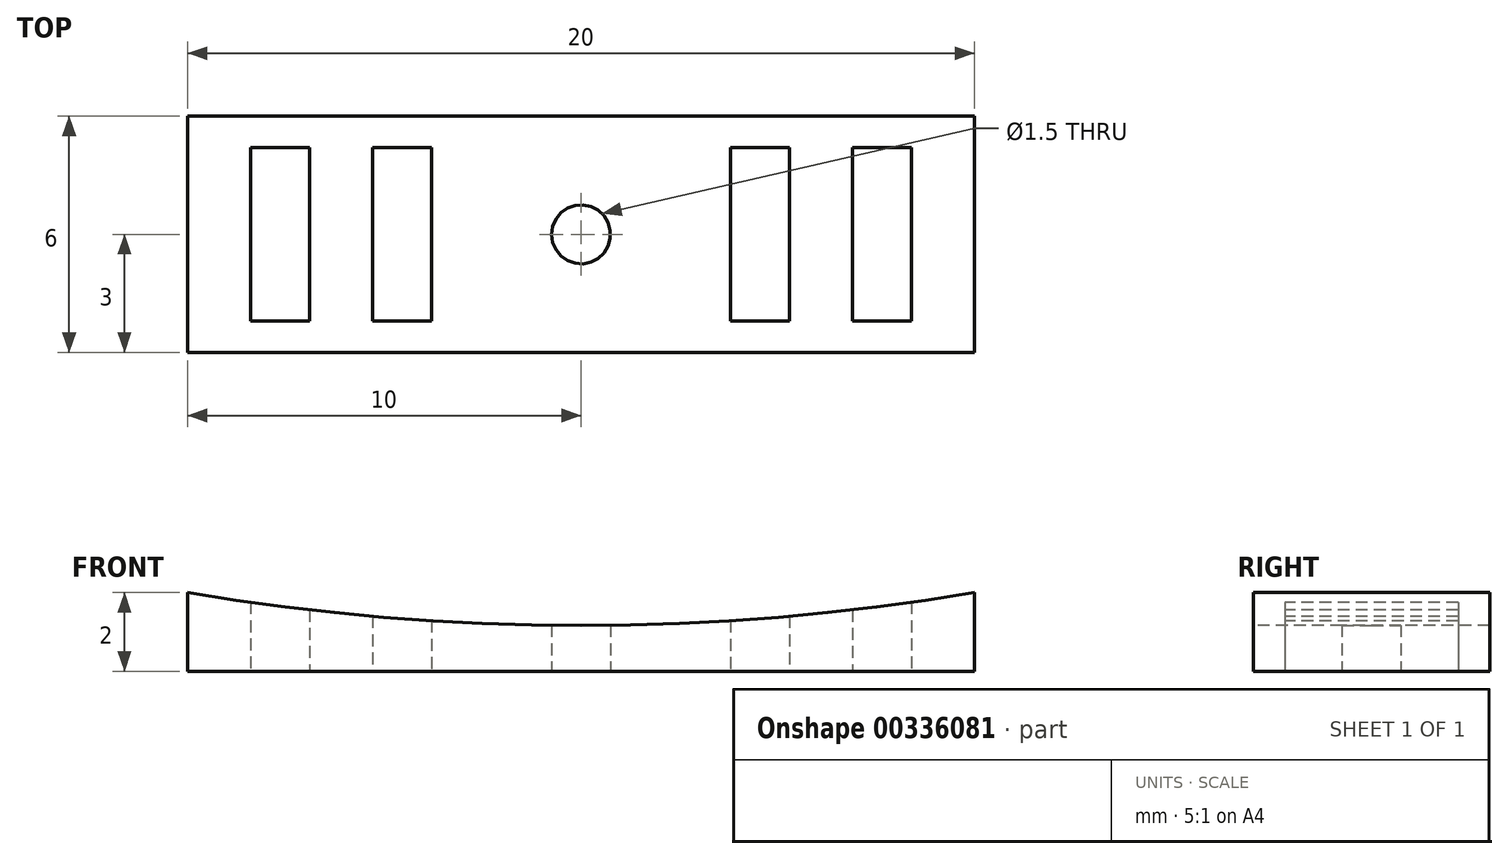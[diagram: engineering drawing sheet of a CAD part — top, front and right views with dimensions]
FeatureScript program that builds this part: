
annotation { "Feature Type Name" : "Feature", "Feature Type Description" : "" }
export const myFeature = defineFeature(function(context is Context, id is Id, definition is map)
    precondition{}
    {
        {
            var Q0;
            Q0=qCreatedBy(makeId("Front.planeOp"),FACE);
            var sketch = newSketch(context, id + "F0", { "sketchPlane" : qUnion([Q0])});
            skLineSegment(sketch, "E0.bottom", {"start": v(0, 0) * mm, "end": v(20, 0) * mm});
            skLineSegment(sketch, "E0.top", {"start": v(0, 2) * mm, "end": v(20, 2) * mm, "construction": true});
            skLineSegment(sketch, "E0.left", {"start": v(0, 0) * mm, "end": v(0, 2) * mm});
            skLineSegment(sketch, "E0.right", {"start": v(20, 0) * mm, "end": v(20, 2) * mm});
            skArc(sketch, "E1", {"start": v(0, 2) * mm, "mid": v(10, 1.16) * mm, "end": v(20, 2) * mm});
            skSolve(sketch);
        }
        {
            var Q0;
            Q0 = qSketchRegion(id + "F0", true);
            extrude(context, id + "F1", {"entities" : qUnion([Q0]), "oppositeDirection" : true, "depth" : 6 * mm});
        }
        {
            var Q0;
            Q0=makeQuery(id+"F1.opExtrude","SWEPT_FACE",FACE,{"disambiguationData":[OSD([sQuery(id+"F0.wireOp",EDGE,"E0.bottom")])]});
            var sketch = newSketch(context, id + "F2", { "sketchPlane" : qUnion([Q0])});
            skLineSegment(sketch, "E2", {"start": v(10, 0) * mm, "end": v(10, -6) * mm, "construction": true});
            skPoint(sketch, "E3", {"position": v(10, -3) * mm});
            skLineSegment(sketch, "E4", {"start": v(5, -2.5) * mm, "end": v(5, 0) * mm, "construction": true});
            skLineSegment(sketch, "E5", {"start": v(15, -2.5) * mm, "end": v(15, 0) * mm, "construction": true});
            skCircle(sketch, "E6", {"center": v(10, -3) * mm, "radius": 0.75 * mm});
            skLineSegment(sketch, "E7", {"start": v(5, -2.5) * mm, "end": v(15, -2.5) * mm, "construction": true});
            skLineSegment(sketch, "E8", {"start": v(0, -3) * mm, "end": v(20, -3) * mm, "construction": true});
            skSolve(sketch);
        }
        {
            var Q0;
            Q0=makeQuery(id+"F2.imprint","IMPRINT",FACE,{"disambiguationData":[TD([[makeQuery(id+"F2.imprint","IMPRINT",EDGE,{"derivedFrom":sQuery(id+"F2.wireOp",EDGE,"E6")}),1.0]])]});
            var Q1;
            Q1=sQuery(id+"F2.wireOp",EDGE,"E6");
            extrude(context, id + "F3", {"entities" : qUnion([Q0]), "operationType" : NewBodyOperationType.REMOVE, "surfaceEntities" : qUnion([Q1]), "oppositeDirection" : true, "depth" : 25 * mm});
        }
        {
            var Q0;
            Q0=makeQuery(id+"F1.opExtrude","SWEPT_FACE",FACE,{"disambiguationData":[OSD([sQuery(id+"F0.wireOp",EDGE,"E0.bottom")])]});
            var sketch = newSketch(context, id + "F4", { "sketchPlane" : qUnion([Q0])});
            skLineSegment(sketch, "E9", {"start": v(0, -3) * mm, "end": v(20, -3) * mm, "construction": true});
            skLineSegment(sketch, "E10", {"start": v(10, -3) * mm, "end": v(10, 0) * mm, "construction": true});
            skLineSegment(sketch, "E11", {"start": v(0, -3) * mm, "end": v(10, 0) * mm, "construction": true});
            skLineSegment(sketch, "E12", {"start": v(0, 0) * mm, "end": v(10, -3) * mm, "construction": true});
            skLineSegment(sketch, "E13", {"start": v(10, -3) * mm, "end": v(20, 0) * mm, "construction": true});
            skLineSegment(sketch, "E14", {"start": v(20, 0) * mm, "end": v(20, -3) * mm, "construction": true});
            skLineSegment(sketch, "E15", {"start": v(10, 0) * mm, "end": v(20, -3) * mm, "construction": true});
            skLineSegment(sketch, "E16.bottom", {"start": v(3.1, -5.2) * mm, "end": v(1.6, -5.2) * mm});
            skLineSegment(sketch, "E16.top", {"start": v(3.1, -0.8) * mm, "end": v(1.6, -0.8) * mm});
            skLineSegment(sketch, "E16.left", {"start": v(3.1, -5.2) * mm, "end": v(3.1, -0.8) * mm});
            skLineSegment(sketch, "E16.right", {"start": v(1.6, -5.2) * mm, "end": v(1.6, -0.8) * mm});
            skPoint(sketch, "E16.middle", {"position": v(2.35, -3) * mm});
            skLineSegment(sketch, "E17.bottom", {"start": v(6.2, -5.2) * mm, "end": v(4.7, -5.2) * mm});
            skLineSegment(sketch, "E17.top", {"start": v(6.2, -0.8) * mm, "end": v(4.7, -0.8) * mm});
            skLineSegment(sketch, "E17.left", {"start": v(6.2, -5.2) * mm, "end": v(6.2, -0.8) * mm});
            skLineSegment(sketch, "E17.right", {"start": v(4.7, -5.2) * mm, "end": v(4.7, -0.8) * mm});
            skPoint(sketch, "E17.middle", {"position": v(5.45, -3) * mm});
            skLineSegment(sketch, "E18.bottom", {"start": v(13.8, -5.2) * mm, "end": v(15.3, -5.2) * mm});
            skLineSegment(sketch, "E18.top", {"start": v(13.8, -0.8) * mm, "end": v(15.3, -0.8) * mm});
            skLineSegment(sketch, "E18.left", {"start": v(13.8, -5.2) * mm, "end": v(13.8, -0.8) * mm});
            skLineSegment(sketch, "E18.right", {"start": v(15.3, -5.2) * mm, "end": v(15.3, -0.8) * mm});
            skPoint(sketch, "E18.middle", {"position": v(14.55, -3) * mm});
            skLineSegment(sketch, "E19.bottom", {"start": v(16.9, -5.2) * mm, "end": v(18.4, -5.2) * mm});
            skLineSegment(sketch, "E19.top", {"start": v(16.9, -0.8) * mm, "end": v(18.4, -0.8) * mm});
            skLineSegment(sketch, "E19.left", {"start": v(16.9, -5.2) * mm, "end": v(16.9, -0.8) * mm});
            skLineSegment(sketch, "E19.right", {"start": v(18.4, -5.2) * mm, "end": v(18.4, -0.8) * mm});
            skPoint(sketch, "E19.middle", {"position": v(17.65, -3) * mm});
            skSolve(sketch);
        }
        {
            var Q0;
            Q0=makeQuery(id+"F4.imprint","IMPRINT",FACE,{"disambiguationData":[TD([[makeQuery(id+"F4.imprint","IMPRINT",EDGE,{"derivedFrom":sQuery(id+"F4.wireOp",EDGE,"E17.bottom")}),-1.0]])]});
            var Q1;
            Q1=makeQuery(id+"F4.imprint","IMPRINT",FACE,{"disambiguationData":[TD([[makeQuery(id+"F4.imprint","IMPRINT",EDGE,{"derivedFrom":sQuery(id+"F4.wireOp",EDGE,"E16.bottom")}),-1.0]])]});
            var Q2;
            Q2=makeQuery(id+"F4.imprint","IMPRINT",FACE,{"disambiguationData":[TD([[makeQuery(id+"F4.imprint","IMPRINT",EDGE,{"derivedFrom":sQuery(id+"F4.wireOp",EDGE,"E18.bottom")}),1.0]])]});
            var Q3;
            Q3=makeQuery(id+"F4.imprint","IMPRINT",FACE,{"disambiguationData":[TD([[makeQuery(id+"F4.imprint","IMPRINT",EDGE,{"derivedFrom":sQuery(id+"F4.wireOp",EDGE,"E19.bottom")}),1.0]])]});
            extrude(context, id + "F5", {"entities" : qUnion([Q0, Q1, Q2, Q3]), "operationType" : NewBodyOperationType.REMOVE, "oppositeDirection" : true, "depth" : 25 * mm});
        }
    });
